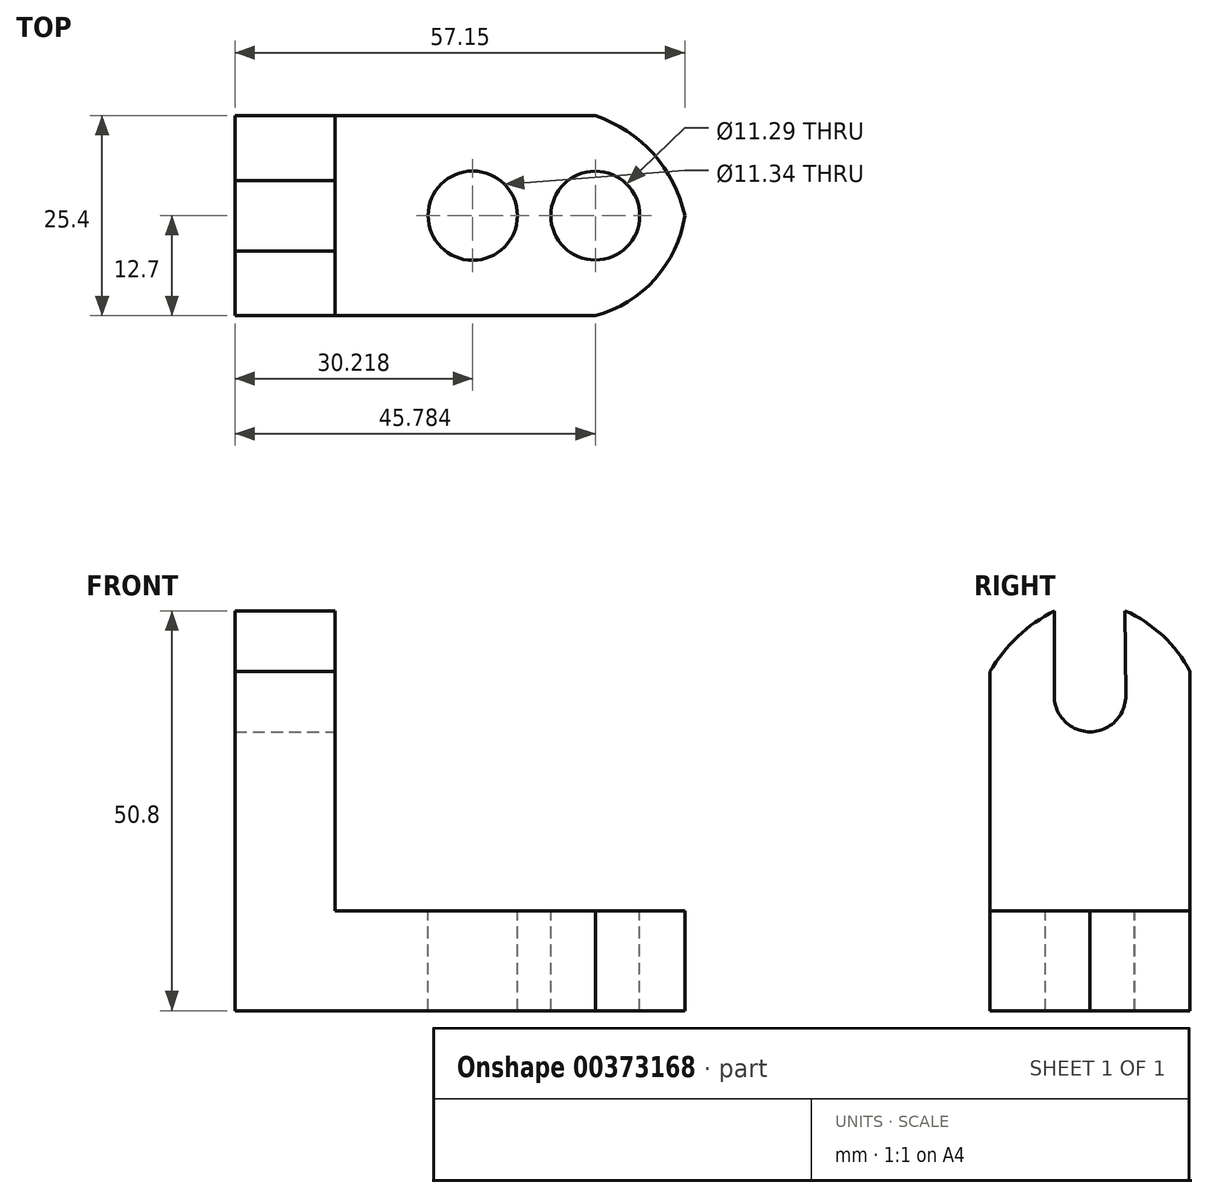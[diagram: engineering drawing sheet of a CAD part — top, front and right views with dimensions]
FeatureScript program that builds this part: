
annotation { "Feature Type Name" : "Feature", "Feature Type Description" : "" }
export const myFeature = defineFeature(function(context is Context, id is Id, definition is map)
    precondition{}
    {
        {
            var Q0;
            Q0=qCreatedBy(makeId("Front.planeOp"),FACE);
            var sketch = newSketch(context, id + "F0", { "sketchPlane" : qUnion([Q0])});
            skLineSegment(sketch, "E0", {"start": v(0, 0) * mm, "end": v(0, 50.8) * mm});
            skLineSegment(sketch, "E1", {"start": v(0, 50.8) * mm, "end": v(12.7, 50.8) * mm});
            skLineSegment(sketch, "E2", {"start": v(12.7, 50.8) * mm, "end": v(12.7, 12.7) * mm});
            skLineSegment(sketch, "E3", {"start": v(12.7, 12.7) * mm, "end": v(57.15, 12.7) * mm});
            skLineSegment(sketch, "E4", {"start": v(57.15, 12.7) * mm, "end": v(57.15, 0) * mm});
            skLineSegment(sketch, "E5", {"start": v(57.15, 0) * mm, "end": v(0, 0) * mm});
            skSolve(sketch);
        }
        {
            var Q0;
            Q0=makeQuery(id+"F0.imprint","IMPRINT",FACE,{"disambiguationData":[TD([[makeQuery(id+"F0.imprint","IMPRINT",EDGE,{"derivedFrom":sQuery(id+"F0.wireOp",EDGE,"E0")}),-1.0]])]});
            extrude(context, id + "F1", {"entities" : qUnion([Q0]), "depth" : 25.4 * mm});
        }
        {
            var Q0;
            Q0=makeQuery(id+"F1.opExtrude","SWEPT_FACE",FACE,{"disambiguationData":[OSD([sQuery(id+"F0.wireOp",EDGE,"E2")])]});
            var sketch = newSketch(context, id + "F2", { "sketchPlane" : qUnion([Q0])});
            skPoint(sketch, "E6.centerSnap0", {"position": v(-12.7, 50.8) * mm});
            skCircle(sketch, "E7", {"center": v(-12.7, 39.96) * mm, "radius": 4.53 * mm});
            skLineSegment(sketch, "E8", {"start": v(-17.23, 39.96) * mm, "end": v(-17.23, 50.8) * mm});
            skLineSegment(sketch, "E9", {"start": v(-8.17, 40) * mm, "end": v(-8.26, 50.8) * mm});
            skArc(sketch, "E10", {"start": v(-17.23, 50.8) * mm, "mid": v(-21.88, 47.53) * mm, "end": v(-25.4, 43.07) * mm});
            skArc(sketch, "E11", {"start": v(0, 43.07) * mm, "mid": v(-3.47, 47.64) * mm, "end": v(-8.26, 50.8) * mm});
            skSolve(sketch);
        }
        {
            var Q0;
            Q0 = qSketchRegion(id + "F2", true);
            var Q1;
            {var subQ0=sQuery(id+"F2.wireOp",EDGE,"E10");Q1=makeQuery(id+"F2.imprint","IMPRINT",FACE,{"disambiguationData":[TD([[makeQuery(id+"F2.imprint","IMPRINT",EDGE,{"derivedFrom":subQ0}),-1.0]])]});}
            var Q2;
            {var subQ0=sQuery(id+"F2.wireOp",EDGE,"E8");Q2=makeQuery(id+"F2.imprint","IMPRINT",FACE,{"disambiguationData":[TD([[makeQuery(id+"F2.imprint","IMPRINT",EDGE,{"derivedFrom":subQ0}),-1.0]])]});}
            var Q3;
            {var subQ0=sQuery(id+"F2.wireOp",EDGE,"E11");Q3=makeQuery(id+"F2.imprint","IMPRINT",FACE,{"disambiguationData":[TD([[makeQuery(id+"F2.imprint","IMPRINT",EDGE,{"derivedFrom":subQ0}),-1.0]])]});}
            extrude(context, id + "F3", {"entities" : qUnion([Q0, Q1, Q2, Q3]), "operationType" : NewBodyOperationType.REMOVE, "oppositeDirection" : true, "depth" : 25.4 * mm});
        }
        {
            var Q0;
            Q0=makeQuery(id+"F1.opExtrude","SWEPT_FACE",FACE,{"disambiguationData":[OSD([sQuery(id+"F0.wireOp",EDGE,"E3")])]});
            var sketch = newSketch(context, id + "F4", { "sketchPlane" : qUnion([Q0])});
            skCircle(sketch, "E12", {"center": v(44.68, -12.7) * mm, "radius": 6.3 * mm});
            skPoint(sketch, "E12.centerSnap0", {"position": v(57.15, -12.7) * mm});
            skCircle(sketch, "E13", {"center": v(26.81, -12.7) * mm, "radius": 6.28 * mm});
            skArc(sketch, "E14", {"start": v(57.15, -12.7) * mm, "mid": v(52.53, -4.76) * mm, "end": v(44.68, 0) * mm});
            skArc(sketch, "E15", {"start": v(44.68, -25.4) * mm, "mid": v(52.53, -20.63) * mm, "end": v(57.15, -12.7) * mm});
            skSolve(sketch);
        }
        {
            var Q0;
            {var subQ0=sQuery(id+"F4.wireOp",EDGE,"E14");Q0=makeQuery(id+"F4.imprint","IMPRINT",FACE,{"disambiguationData":[TD([[makeQuery(id+"F4.imprint","IMPRINT",EDGE,{"derivedFrom":subQ0}),-1.0]])]});}
            var Q1;
            {var subQ0=sQuery(id+"F4.wireOp",EDGE,"E15");Q1=makeQuery(id+"F4.imprint","IMPRINT",FACE,{"disambiguationData":[TD([[makeQuery(id+"F4.imprint","IMPRINT",EDGE,{"derivedFrom":subQ0}),-1.0]])]});}
            extrude(context, id + "F5", {"entities" : qUnion([Q0, Q1]), "operationType" : NewBodyOperationType.REMOVE, "depth" : 25.4 * mm});
        }
        {
            var Q0;
            Q0=makeQuery(id+"F1.opExtrude","SWEPT_FACE",FACE,{"disambiguationData":[OSD([sQuery(id+"F0.wireOp",EDGE,"E3")])]});
            var sketch = newSketch(context, id + "F6", { "sketchPlane" : qUnion([Q0])});
            skCircle(sketch, "E16", {"center": v(45.78, -12.7) * mm, "radius": 5.65 * mm});
            skPoint(sketch, "E16.centerSnap0", {"position": v(57.15, -12.7) * mm});
            skCircle(sketch, "E17", {"center": v(30.22, -12.7) * mm, "radius": 5.67 * mm});
            skArc(sketch, "E18", {"start": v(57.15, -12.7) * mm, "mid": v(53.15, -4.85) * mm, "end": v(45.78, 0) * mm});
            skArc(sketch, "E19", {"start": v(45.78, -25.4) * mm, "mid": v(53.37, -20.75) * mm, "end": v(57.15, -12.7) * mm});
            skSolve(sketch);
        }
        {
            var Q0;
            Q0 = qSketchRegion(id + "F6", true);
            var Q1;
            {var subQ0=sQuery(id+"F6.wireOp",EDGE,"E18");Q1=makeQuery(id+"F6.imprint","IMPRINT",FACE,{"disambiguationData":[TD([[makeQuery(id+"F6.imprint","IMPRINT",EDGE,{"derivedFrom":subQ0}),-1.0]])]});}
            var Q2;
            {var subQ0=sQuery(id+"F6.wireOp",EDGE,"E19");Q2=makeQuery(id+"F6.imprint","IMPRINT",FACE,{"disambiguationData":[TD([[makeQuery(id+"F6.imprint","IMPRINT",EDGE,{"derivedFrom":subQ0}),-1.0]])]});}
            extrude(context, id + "F7", {"entities" : qUnion([Q0, Q1, Q2]), "operationType" : NewBodyOperationType.REMOVE, "oppositeDirection" : true, "depth" : 25.4 * mm});
        }
    });
